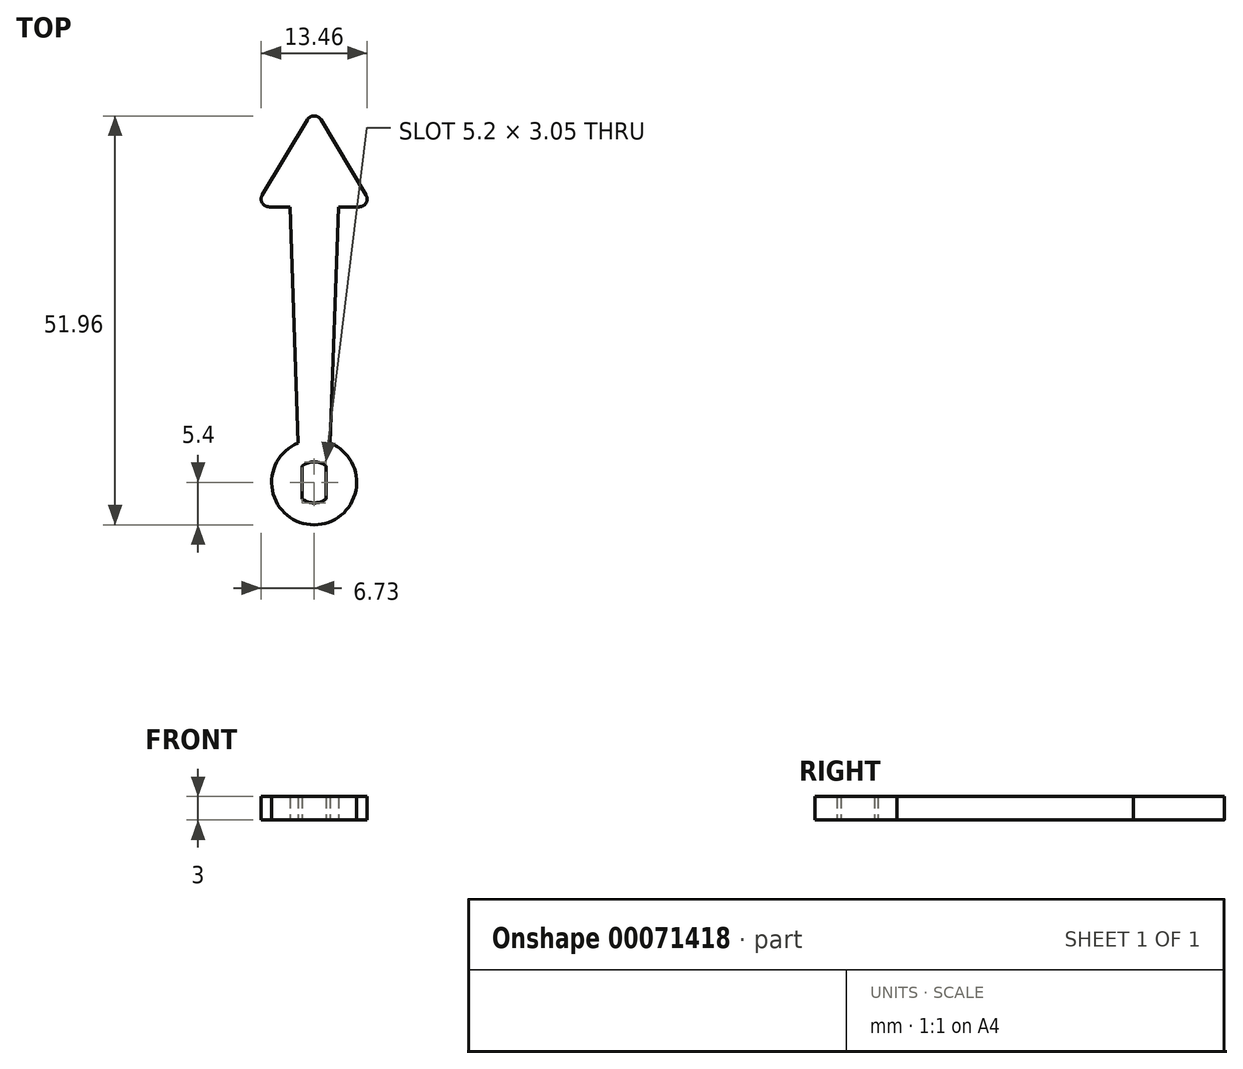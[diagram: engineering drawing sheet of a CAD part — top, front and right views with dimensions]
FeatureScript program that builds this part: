
annotation { "Feature Type Name" : "Feature", "Feature Type Description" : "" }
export const myFeature = defineFeature(function(context is Context, id is Id, definition is map)
    precondition{}
    {
        {
            var Q0;
            Q0=qCreatedBy(makeId("Top.planeOp"),FACE);
            var sketch = newSketch(context, id + "F0", { "sketchPlane" : qUnion([Q0])});
            skCircle(sketch, "E0", {"center": v(0, 0) * mm, "radius": 2.6 * mm});
            skCircle(sketch, "E1", {"center": v(0, 0) * mm, "radius": 5.4 * mm});
            skLineSegment(sketch, "E2", {"start": v(-1.53, 2.1) * mm, "end": v(-1.53, -2.1) * mm});
            skLineSegment(sketch, "E3", {"start": v(1.52, 2.1) * mm, "end": v(1.52, -2.1) * mm});
            skSolve(sketch);
        }
        {
            var Q0;
            {var subQ0=sQuery(id+"F0.wireOp",EDGE,"E2");Q0=makeQuery(id+"F0.imprint","IMPRINT",FACE,{"disambiguationData":[TD([[makeQuery(id+"F0.imprint","IMPRINT",EDGE,{"derivedFrom":subQ0}),-1.0]])]});}
            var Q1;
            {var subQ0=sQuery(id+"F0.wireOp",EDGE,"E3");Q1=makeQuery(id+"F0.imprint","IMPRINT",FACE,{"disambiguationData":[TD([[makeQuery(id+"F0.imprint","IMPRINT",EDGE,{"derivedFrom":subQ0}),1.0]])]});}
            var Q2;
            Q2=makeQuery(id+"F0.imprint","IMPRINT",FACE,{"disambiguationData":[TD([[makeQuery(id+"F0.imprint","IMPRINT",EDGE,{"derivedFrom":sQuery(id+"F0.wireOp",EDGE,"E1")}),1.0]])]});
            extrude(context, id + "F1", {"entities" : qUnion([Q0, Q1, Q2]), "endBound" : BoundingType.SYMMETRIC, "depth" : 3 * mm});
        }
        {
            var Q0;
            Q0=qCreatedBy(makeId("Top.planeOp"),FACE);
            var sketch = newSketch(context, id + "F2", { "sketchPlane" : qUnion([Q0])});
            skLineSegment(sketch, "E4", {"start": v(0, 0) * mm, "end": v(0, 35) * mm, "construction": true});
            skLineSegment(sketch, "E5", {"start": v(0, 35) * mm, "end": v(3.08, 35) * mm});
            skLineSegment(sketch, "E6", {"start": v(0, 4.07) * mm, "end": v(2, 4.07) * mm});
            skLineSegment(sketch, "E7", {"start": v(3.08, 35) * mm, "end": v(2, 4.07) * mm});
            skLineSegment(sketch, "E8.MirrorCS", {"start": v(-3.08, 35) * mm, "end": v(-2, 4.07) * mm});
            skLineSegment(sketch, "E9.MirrorCS", {"start": v(0, 4.07) * mm, "end": v(-2, 4.07) * mm});
            skLineSegment(sketch, "E10.MirrorCS", {"start": v(0, 35) * mm, "end": v(-3.08, 35) * mm});
            skSolve(sketch);
        }
        {
            var Q0;
            Q0 = qSketchRegion(id + "F2", true);
            var Q1;
            Q1=makeQuery(id+"F1.opExtrude","CAP_FACE",FACE,{"disambiguationData":[OSD([sQuery(id+"F0.wireOp",EDGE,"E0"),sQuery(id+"F0.wireOp",EDGE,"E1"),sQuery(id+"F0.wireOp",EDGE,"E2"),sQuery(id+"F0.wireOp",EDGE,"E3")])],"isStart":false});
            extrude(context, id + "F3", {"entities" : qUnion([Q0]), "operationType" : NewBodyOperationType.ADD, "endBound" : BoundingType.SYMMETRIC, "endBoundEntityFace" : qUnion([Q1]), "depth" : 3 * mm});
        }
        {
            var Q0;
            Q0=makeQuery(id+"F3.boolean.opBoolean","MERGE",FACE,{"derivedFrom":[makeQuery(id+"F1.opExtrude","CAP_FACE",FACE,{"disambiguationData":[OSD([sQuery(id+"F0.wireOp",EDGE,"E0"),sQuery(id+"F0.wireOp",EDGE,"E1"),sQuery(id+"F0.wireOp",EDGE,"E2"),sQuery(id+"F0.wireOp",EDGE,"E3")])],"isStart":false}),makeQuery(id+"F3.opExtrude","CAP_FACE",FACE,{"disambiguationData":[OSD([sQuery(id+"F2.wireOp",EDGE,"E5"),sQuery(id+"F2.wireOp",EDGE,"E6"),sQuery(id+"F2.wireOp",EDGE,"E7"),sQuery(id+"F2.wireOp",EDGE,"E8.MirrorCS"),sQuery(id+"F2.wireOp",EDGE,"E9.MirrorCS"),sQuery(id+"F2.wireOp",EDGE,"E10.MirrorCS")])],"isStart":false})]});
            var sketch = newSketch(context, id + "F4", { "sketchPlane" : qUnion([Q0])});
            skLineSegment(sketch, "E11", {"start": v(0, 35) * mm, "end": v(0, 47.5) * mm, "construction": true});
            skLineSegment(sketch, "E12", {"start": v(-7.5, 35) * mm, "end": v(7.5, 35) * mm});
            skLineSegment(sketch, "E13", {"start": v(-7.5, 35) * mm, "end": v(0, 47.5) * mm});
            skLineSegment(sketch, "E14", {"start": v(7.5, 35) * mm, "end": v(0, 47.5) * mm});
            skSolve(sketch);
        }
        {
            var Q0;
            {var subQ0=sQuery(id+"F4.wireOp",EDGE,"E13");Q0=makeQuery(id+"F4.imprint","IMPRINT",FACE,{"disambiguationData":[TD([[makeQuery(id+"F4.imprint","IMPRINT",EDGE,{"derivedFrom":subQ0}),-1.0]])]});}
            var Q1;
            Q1=makeQuery(id+"F3.boolean.opBoolean","MERGE",FACE,{"derivedFrom":[makeQuery(id+"F1.opExtrude","CAP_FACE",FACE,{"disambiguationData":[OSD([sQuery(id+"F0.wireOp",EDGE,"E0"),sQuery(id+"F0.wireOp",EDGE,"E1"),sQuery(id+"F0.wireOp",EDGE,"E2"),sQuery(id+"F0.wireOp",EDGE,"E3")])],"isStart":true}),makeQuery(id+"F3.opExtrude","CAP_FACE",FACE,{"disambiguationData":[OSD([sQuery(id+"F2.wireOp",EDGE,"E5"),sQuery(id+"F2.wireOp",EDGE,"E6"),sQuery(id+"F2.wireOp",EDGE,"E7"),sQuery(id+"F2.wireOp",EDGE,"E8.MirrorCS"),sQuery(id+"F2.wireOp",EDGE,"E9.MirrorCS"),sQuery(id+"F2.wireOp",EDGE,"E10.MirrorCS")])],"isStart":true})]});
            extrude(context, id + "F5", {"entities" : qUnion([Q0]), "operationType" : NewBodyOperationType.ADD, "endBound" : BoundingType.UP_TO_SURFACE, "oppositeDirection" : true, "endBoundEntityFace" : qUnion([Q1]), "depth" : 25 * mm});
        }
        {
            var Q0;
            Q0=makeQuery(id+"F5.opExtrude","SWEPT_EDGE",EDGE,{"disambiguationData":[OSD([sQuery(id+"F4.wireOp",EDGE,"E12"),sQuery(id+"F4.wireOp",EDGE,"E13")])]});
            var Q1;
            Q1=makeQuery(id+"F5.opExtrude","SWEPT_EDGE",EDGE,{"disambiguationData":[OSD([sQuery(id+"F4.wireOp",EDGE,"E13"),sQuery(id+"F4.wireOp",EDGE,"E14")])]});
            var Q2;
            Q2=makeQuery(id+"F5.opExtrude","SWEPT_EDGE",EDGE,{"disambiguationData":[OSD([sQuery(id+"F4.wireOp",EDGE,"E12"),sQuery(id+"F4.wireOp",EDGE,"E14")])]});
            fillet(context, id + "F6", {"entities" : qUnion([Q0, Q1, Q2]), "radius" : 1 * mm, "tangentPropagation" : true, "allowEdgeOverflow" : false});
        }
    });
